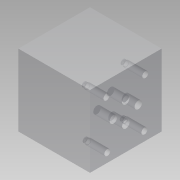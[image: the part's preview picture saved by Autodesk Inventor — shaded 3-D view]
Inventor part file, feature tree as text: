
AUTODESK INVENTOR PART (.ipt)
format: ipt  version: 2014 (Build 180170000, 170)  size: 211,968 bytes
history: native  units: mm
features: other x48, extrude x17, sketch x17
ambient origin geometry x8: Origin, YZ Plane, XZ Plane, XY Plane, X Axis, Y Axis, Z Axis, Center Point
bodies: 实体1 (feature_tree)
feature tree (82):
  extrude  "拉伸1"  Depth=51.0mm
  other  "UCS1"
  other  "UCS2"
  other  "UCS3"
  other  "UCS4"
  other  "UCS5"
  other  "UCS6"
  extrude  "拉伸2"  Depth=30.0mm
  extrude  "拉伸3"  Depth=4.25mm
  extrude  "拉伸4"  Depth=21.5mm
  extrude  "拉伸5"  Depth=0.75mm
  extrude  "拉伸6"  TaperAngle=0.0deg  [1 undecoded]
  extrude  "拉伸7"  Depth=31.75mm
  extrude  "拉伸8"  Depth=18.5mm
  extrude  "拉伸9"  Depth=18.5mm
  extrude  "拉伸10"  Depth=5.0mm
  extrude  "拉伸11"  Depth=12.7mm
  extrude  "拉伸12"  Depth=12.7mm
  extrude  "拉伸13"  Depth=12.7mm
  extrude  "拉伸14"  Depth=10.7mm TaperAngle=0.0deg
  extrude  "拉伸15"  Depth=10.7mm
  extrude  "拉伸16"  Depth=12.7mm
  extrude  "拉伸17"  Depth=12.7mm
  sketch  "草图1"  dims[d0=60.0mm d1=0.0mm]
  sketch  "草图2"  dims[d2=0.0mm d3=0.0mm d4=0.0mm d5=0.0mm d6=0.0mm d7=0.0mm]
  sketch  "草图3"  dims[d8=0.0mm d9=0.0mm d10=0.0mm d11=0.0mm d12=0.0mm d13=0.0mm]
  sketch  "草图4"  dims[d14=0.0mm d15=0.0mm d16=0.0mm d17=0.0mm d18=0.0mm d19=0.0mm]
  sketch  "草图5"  dims[d20=0.0mm d21=0.0mm d22=0.0mm d23=0.0mm d24=0.0mm d25=0.0mm]
  sketch  "草图6"  dims[d26=0.0mm d27=0.0mm d28=0.0mm d29=0.0mm d30=0.0mm d31=0.0mm]
  sketch  "草图7"  dims[d32=0.0mm d33=0.0mm d34=0.0mm d35=0.0mm d36=0.0mm d37=0.0mm d38=51.0mm]
  sketch  "草图8"  dims[d39=43.0mm d40=30.0mm]
  sketch  "草图9"  dims[d41=29.0mm d42=4.25mm]
  sketch  "草图10"  dims[d43=15.5mm d44=21.5mm]
  sketch  "草图11"  dims[d45=40.5mm d46=0.75mm]
  sketch  "草图12"  dims[d47=40.5mm d49=0.0mm]
  sketch  "草图13"  dims[d50=31.0mm d51=31.75mm]
  sketch  "草图14"  dims[d52=18.5mm d53=0.0mm d54=18.5mm d55=-10.297443mm]
  sketch  "草图15"  dims[d56=18.5mm d57=-10.297443mm d58=18.5mm d59=-10.297443mm]
  sketch  "草图17"  dims[d60=18.5mm d61=-10.297443mm d62=5.0mm]
  sketch  "草图18"  dims[d63=16.0mm d64=0.0mm d65=6.3mm d66=25.9mm d67=21.5mm d68=10.7mm d69=0.0mm d70=10.7mm d71=-10.297443mm d72=6.3mm d73=21.5mm d74=5.1mm d75=13.7mm d76=0.0mm d77=13.7mm d78=-10.297443mm d79=6.3mm d80=12.7mm d81=15.5mm d82=11.7mm d83=0.0mm d84=11.7mm d85=-10.297443mm d86=6.3mm d87=15.5mm d88=30.2mm d89=12.7mm d90=0.0mm d91=12.7mm d92=-10.297443mm d106=4.0mm d107=33.0mm d108=31.75mm d109=6.0mm d110=0.0mm d111=6.0mm d112=-10.297443mm]
  other  "UCS1: YZ 平面"
  other  "UCS1: XZ 平面"
  other  "UCS1: XY 平面"
  other  "UCS1: X 轴"
  other  "UCS1: Y 轴"
  other  "UCS1: Z 轴"
  other  "UCS1: 原点"
  other  "UCS2: YZ 平面"
  other  "UCS2: XZ 平面"
  other  "UCS2: XY 平面"
  other  "UCS2: X 轴"
  other  "UCS2: Y 轴"
  other  "UCS2: Z 轴"
  other  "UCS2: 原点"
  other  "UCS3: YZ 平面"
  other  "UCS3: XZ 平面"
  other  "UCS3: XY 平面"
  other  "UCS3: X 轴"
  other  "UCS3: Y 轴"
  other  "UCS3: Z 轴"
  other  "UCS3: 原点"
  other  "UCS4: YZ 平面"
  other  "UCS4: XZ 平面"
  other  "UCS4: XY 平面"
  other  "UCS4: X 轴"
  other  "UCS4: Y 轴"
  other  "UCS4: Z 轴"
  other  "UCS4: 原点"
  other  "UCS5: YZ 平面"
  other  "UCS5: XZ 平面"
  other  "UCS5: XY 平面"
  other  "UCS5: X 轴"
  other  "UCS5: Y 轴"
  other  "UCS5: Z 轴"
  other  "UCS5: 原点"
  other  "UCS6: YZ 平面"
  other  "UCS6: XZ 平面"
  other  "UCS6: XY 平面"
  other  "UCS6: X 轴"
  other  "UCS6: Y 轴"
  other  "UCS6: Z 轴"
  other  "UCS6: 原点"
note: 1 required parameter value undecoded (feature->parameter linkage not recoverable at this tier; creation-order binding heuristic only, values carry confidence <= 0.55)
